# Revit family: 712-5320-001-DN100-300
name_source: partatom
category: Pipe Accessories
units: mm (PartAtom-declared; Revit-internal decimal feet)

## family parameters
Always vertical = Yes
Cut with Voids When Loaded = No
Part Type = Valve - Breaks Into
Round Connector Dimension = Use Diameter
Shared = No
Work Plane-Based = No

## types (8) — shared parameters
Body_wallthickness = 10 mm  [stored 0.0328084 ft]
DN100_PN10/16 = 712-0100-53-201
DN150_PN10/16 = 712-0150-53-201
DN200_PN10 = 712-0200-53-200
DN200_PN16 = 712-0200-53-201
DN250_PN10 = 712-0250-53-200
DN250_PN16 = 712-0250-53-201
DN300_PN10 = 712-0300-53-200
DN300_PN16 = 712-0300-53-201
Description_ = AVK FLANGED PIPE W/LOOSE FLANGES
L = 1000 mm  [stored 3.28084 ft]
Search_Table = 712-5320-001-DN100-300
URL product pages = https://www.avkvalves.com

## per-type parameters (varying)
| type | CH | CH2 | FOD | Flange_thickness | ID | Nominal Diameter (DN) | RF_Thick | Rf_Dia |
| DN100_PN10/16 | 65 mm  [stored 0.213255 ft] | 38 mm  [stored 0.124672 ft] | 110 mm  [stored 0.360892 ft] | 19 mm  [stored 0.062336 ft] | 50 mm  [stored 0.164042 ft] | 100 mm  [stored 0.328084 ft] | 3 mm  [stored 0.00984252 ft] | 78 mm  [stored 0.255906 ft] |
| DN150_PN10/16 | 90 mm  [stored 0.295276 ft] | 40 mm  [stored 0.131234 ft] | 143 mm | 20 mm  [stored 0.0656168 ft] | 75 mm  [stored 0.246063 ft] | 150 mm  [stored 0.492126 ft] | 4 mm  [stored 0.0131234 ft] | 106 mm |
| DN200_PN10 | 115 mm | 40 mm  [stored 0.131234 ft] | 170 mm  [stored 0.557743 ft] | 20 mm  [stored 0.0656168 ft] | 100 mm  [stored 0.328084 ft] | 200 mm  [stored 0.656168 ft] | 4 mm  [stored 0.0131234 ft] | 133 mm  [stored 0.436352 ft] |
| DN250_PN10 | 140 mm  [stored 0.459318 ft] | 44 mm  [stored 0.144357 ft] | 200 mm  [stored 0.656168 ft] | 22 mm  [stored 0.0721785 ft] | 125 mm  [stored 0.410105 ft] | 250 mm  [stored 0.82021 ft] | 4 mm  [stored 0.0131234 ft] | 160 mm  [stored 0.524934 ft] |
| DN250_PN16 | 140 mm  [stored 0.459318 ft] | 44 mm  [stored 0.144357 ft] | 200 mm  [stored 0.656168 ft] | 22 mm  [stored 0.0721785 ft] | 125 mm  [stored 0.410105 ft] | 250 mm  [stored 0.82021 ft] | 4 mm  [stored 0.0131234 ft] | 160 mm  [stored 0.524934 ft] |
| DN200_PN16 | 115 mm | 40 mm  [stored 0.131234 ft] | 170 mm  [stored 0.557743 ft] | 20 mm  [stored 0.0656168 ft] | 100 mm  [stored 0.328084 ft] | 200 mm  [stored 0.656168 ft] | 4 mm  [stored 0.0131234 ft] | 133 mm  [stored 0.436352 ft] |
| DN300_PN10 | 165 mm  [stored 0.541339 ft] | 48 mm  [stored 0.15748 ft] | 228 mm | 24 mm  [stored 0.0787402 ft] | 150 mm  [stored 0.492126 ft] | 300 mm  [stored 0.984252 ft] | 4 mm  [stored 0.0131234 ft] | 185 mm  [stored 0.606955 ft] |
| DN300_PN16 | 165 mm  [stored 0.541339 ft] | 48 mm  [stored 0.15748 ft] | 228 mm | 24 mm  [stored 0.0787402 ft] | 150 mm  [stored 0.492126 ft] | 300 mm  [stored 0.984252 ft] | 4 mm  [stored 0.0131234 ft] | 185 mm  [stored 0.606955 ft] |

note: [stored X ft] marks values corroborated as IEEE doubles in the binary element streams (Revit-internal decimal feet)

## geometry (parser evidence)
native form markers: Sweep x10
no freeform markers — native parametric forms only
